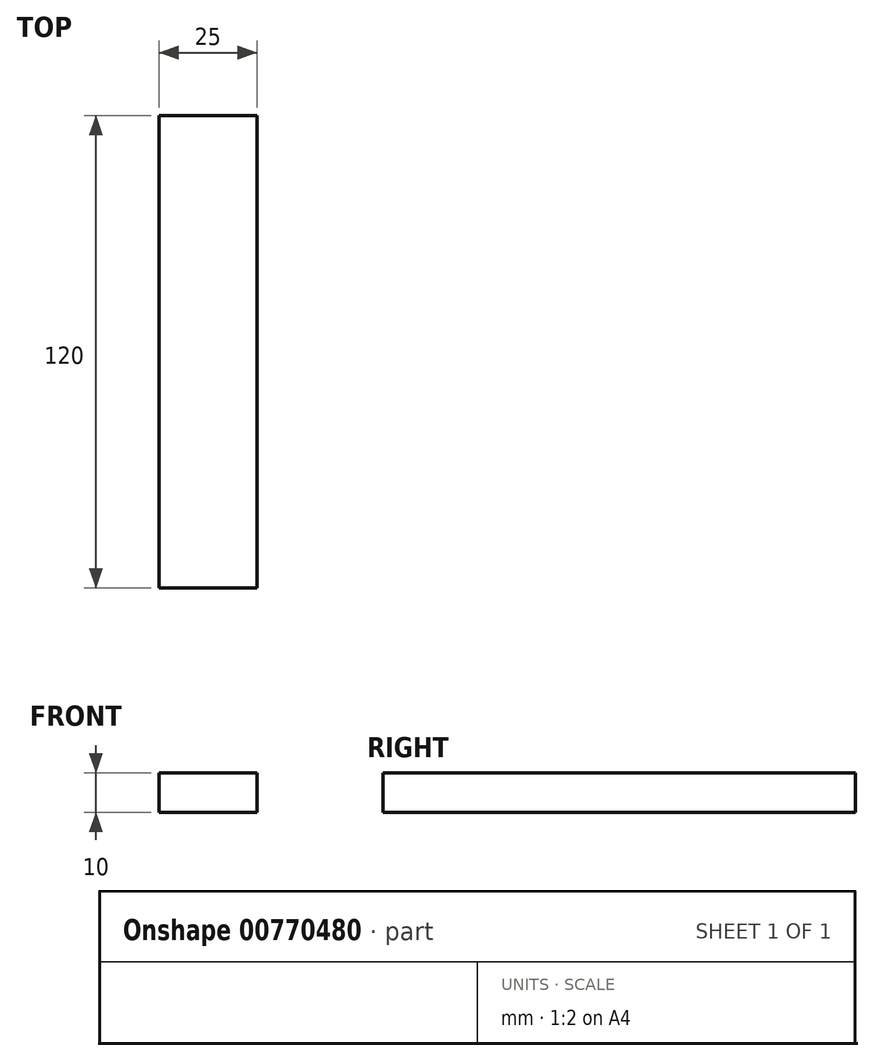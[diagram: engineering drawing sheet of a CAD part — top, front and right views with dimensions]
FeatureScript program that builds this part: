
annotation { "Feature Type Name" : "Feature", "Feature Type Description" : "" }
export const myFeature = defineFeature(function(context is Context, id is Id, definition is map)
    precondition{}
    {
        {
            var Q0;
            Q0=qCreatedBy(makeId("Top.planeOp"),FACE);
            var sketch = newSketch(context, id + "F0", { "sketchPlane" : qUnion([Q0])});
            skLineSegment(sketch, "E0.bottom", {"start": v(-12.5, 60) * mm, "end": v(12.5, 60) * mm});
            skLineSegment(sketch, "E0.top", {"start": v(-12.5, -60) * mm, "end": v(12.5, -60) * mm});
            skLineSegment(sketch, "E0.left", {"start": v(-12.5, 60) * mm, "end": v(-12.5, -60) * mm});
            skLineSegment(sketch, "E0.right", {"start": v(12.5, 60) * mm, "end": v(12.5, -60) * mm});
            skPoint(sketch, "E0.middle", {"position": v(0, 0) * mm});
            skSolve(sketch);
        }
        {
            var Q0;
            Q0 = qSketchRegion(id + "F0", true);
            extrude(context, id + "F1", {"entities" : qUnion([Q0]), "depth" : 10 * mm, "offsetDistance" : 25 * mm});
        }
    });
